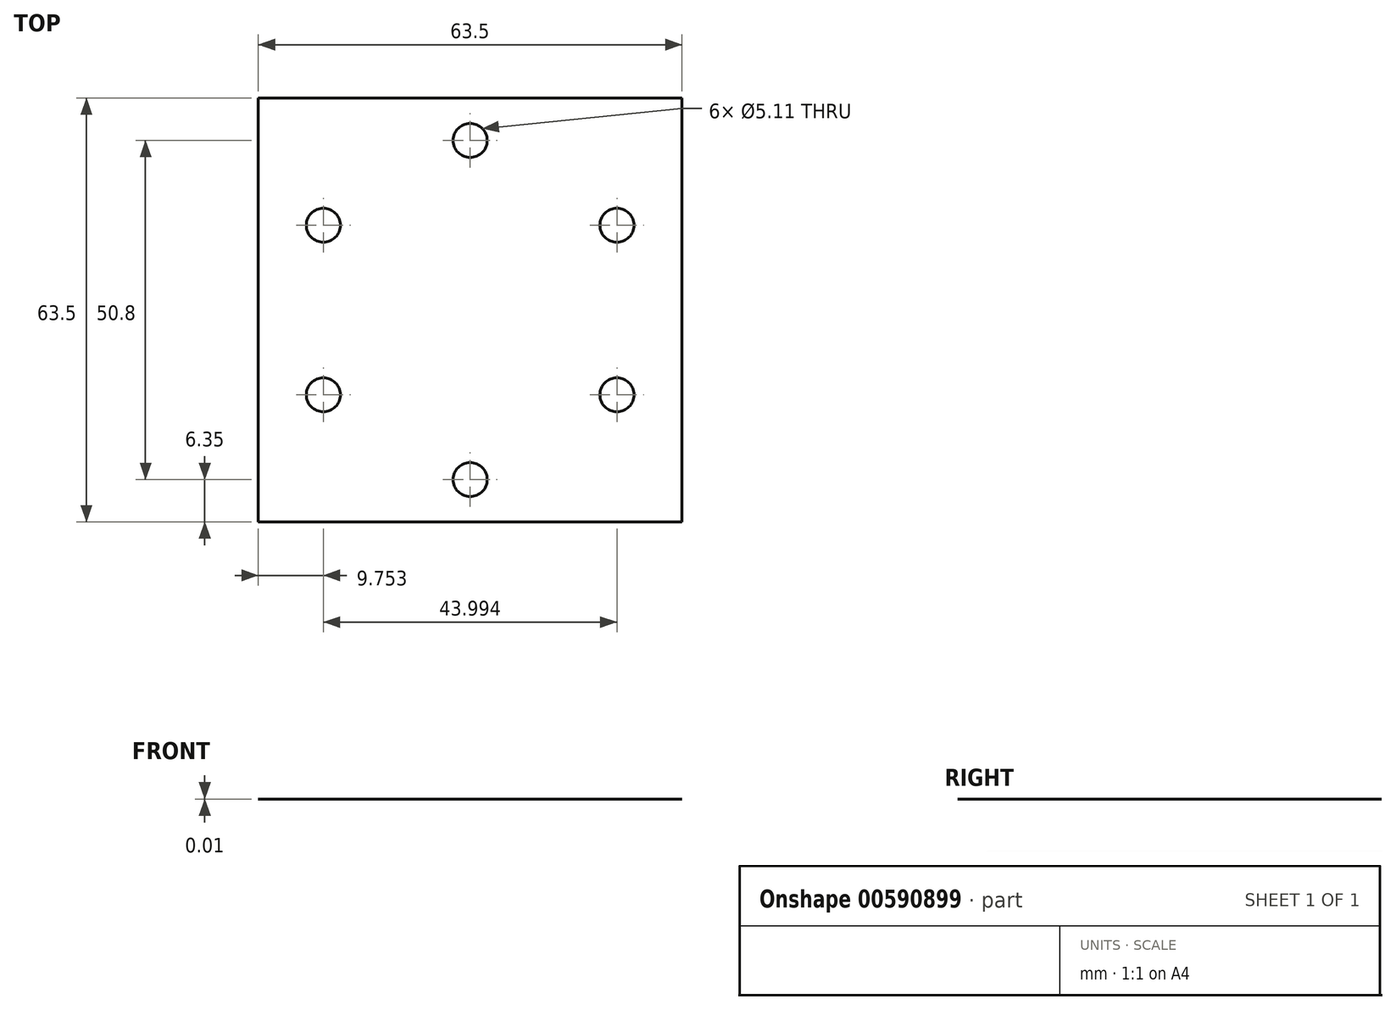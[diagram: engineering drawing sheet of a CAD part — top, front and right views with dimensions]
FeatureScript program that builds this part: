
annotation { "Feature Type Name" : "Feature", "Feature Type Description" : "" }
export const myFeature = defineFeature(function(context is Context, id is Id, definition is map)
    precondition{}
    {
        {
            var Q0;
            Q0=qCreatedBy(makeId("Top.planeOp"),FACE);
            var sketch = newSketch(context, id + "F0", { "sketchPlane" : qUnion([Q0])});
            skLineSegment(sketch, "E0.bottom", {"start": v(31.75, 31.75) * mm, "end": v(-31.75, 31.75) * mm});
            skLineSegment(sketch, "E0.top", {"start": v(31.75, -31.75) * mm, "end": v(-31.75, -31.75) * mm});
            skLineSegment(sketch, "E0.left", {"start": v(31.75, 31.75) * mm, "end": v(31.75, -31.75) * mm});
            skLineSegment(sketch, "E0.right", {"start": v(-31.75, 31.75) * mm, "end": v(-31.75, -31.75) * mm});
            skPoint(sketch, "E0.middle", {"position": v(0, 0) * mm});
            skPoint(sketch, "E1", {"position": v(0, -25.4) * mm});
            skPoint(sketch, "E2.1.0", {"position": v(22, -12.7) * mm});
            skPoint(sketch, "E2.2.0", {"position": v(22, 12.7) * mm});
            skPoint(sketch, "E2.3.0", {"position": v(0, 25.4) * mm});
            skPoint(sketch, "E2.4.0", {"position": v(-22, 12.7) * mm});
            skPoint(sketch, "E2.5.0", {"position": v(-22, -12.7) * mm});
            skLineSegment(sketch, "E2.anchor1", {"start": v(0, 0) * mm, "end": v(0, -25.4) * mm, "construction": true});
            skLineSegment(sketch, "E2.anchor2", {"start": v(0, 0) * mm, "end": v(-22, -12.7) * mm, "construction": true});
            skSolve(sketch);
        }
        {
            var Q0;
            Q0=makeQuery(id+"F0.imprint","IMPRINT",FACE,{"disambiguationData":[TD([[makeQuery(id+"F0.imprint","IMPRINT",EDGE,{"derivedFrom":sQuery(id+"F0.wireOp",EDGE,"E0.bottom")}),1.0]])]});
            extrude(context, id + "F1", {"entities" : qUnion([Q0]), "oppositeDirection" : true, "depth" : 1 / 101.6 * mm, "offsetDistance" : 25 * mm});
        }
        {
            var Q0;
            Q0=sQuery(id+"F0.wireOp",VERTEX,"E1");
            var Q1;
            Q1=sQuery(id+"F0.wireOp",VERTEX,"E2.1.0");
            var Q2;
            Q2=sQuery(id+"F0.wireOp",VERTEX,"E2.2.0");
            var Q3;
            Q3=sQuery(id+"F0.wireOp",VERTEX,"E2.3.0");
            var Q4;
            Q4=sQuery(id+"F0.wireOp",VERTEX,"E2.anchor2.end");
            var Q5;
            Q5=sQuery(id+"F0.wireOp",VERTEX,"E2.4.0");
            var Q6;
            Q6=makeQuery(id+"F1.opExtrude","SWEPT_BODY",BODY,{"disambiguationData":[OSD([sQuery(id+"F0.wireOp",EDGE,"E0.bottom"),sQuery(id+"F0.wireOp",EDGE,"E0.top"),sQuery(id+"F0.wireOp",EDGE,"E0.left"),sQuery(id+"F0.wireOp",EDGE,"E0.right")])]});
            hole(context, id + "F2", {"style" : HoleStyle.SIMPLE, "endStyle" : HoleEndStyle.BLIND, "standardTappedOrClearance" : lookupTablePath({ "standard" : "ANSI", "engagement" : "75%", "pitch" : "20 tpi", "size" : "1/4", "type" : "Tapped" }), "standardBlindInLast" : lookupTablePath({ "standard" : "ANSI", "engagement" : "75%", "pitch" : "20 tpi", "size" : "1/4", "type" : "Tapped" }), "holeDiameter" : 5.1 * mm, "majorDiameter" : 6.35 * mm, "showTappedDepth" : true, "holeDepth" : 4.77 * mm, "isTappedThrough" : true, "tappedDepth" : 3.5 * mm, "tapClearance" : 1, "startFromSketch" : true, "locations" : qUnion([Q0, Q1, Q2, Q3, Q4, Q5]), "scope" : qUnion([Q6])});
        }
    });
